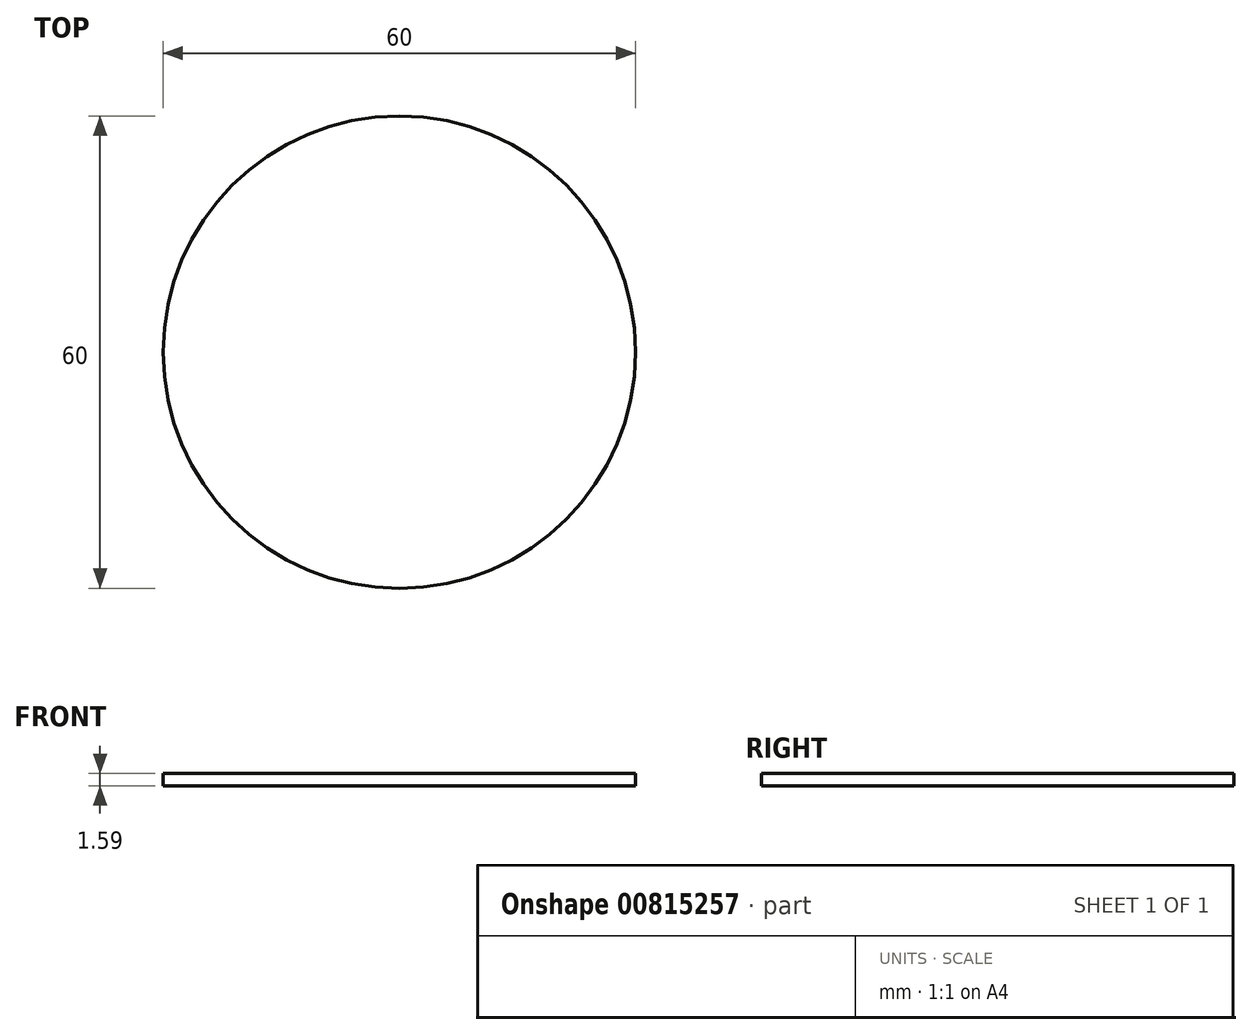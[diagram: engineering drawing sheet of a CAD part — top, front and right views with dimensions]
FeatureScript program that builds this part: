
annotation { "Feature Type Name" : "Feature", "Feature Type Description" : "" }
export const myFeature = defineFeature(function(context is Context, id is Id, definition is map)
    precondition{}
    {
        {
            var Q0;
            Q0=qCreatedBy(makeId("Top.planeOp"),FACE);
            var sketch = newSketch(context, id + "F0", { "sketchPlane" : qUnion([Q0])});
            skCircle(sketch, "E0", {"center": v(0, 0) * mm, "radius": 30 * mm});
            skSolve(sketch);
        }
        {
            var Q0;
            Q0 = qSketchRegion(id + "F0", true);
            extrude(context, id + "F1", {"entities" : qUnion([Q0]), "depth" : 1.59 * mm, "offsetDistance" : 25 * mm});
        }
    });
